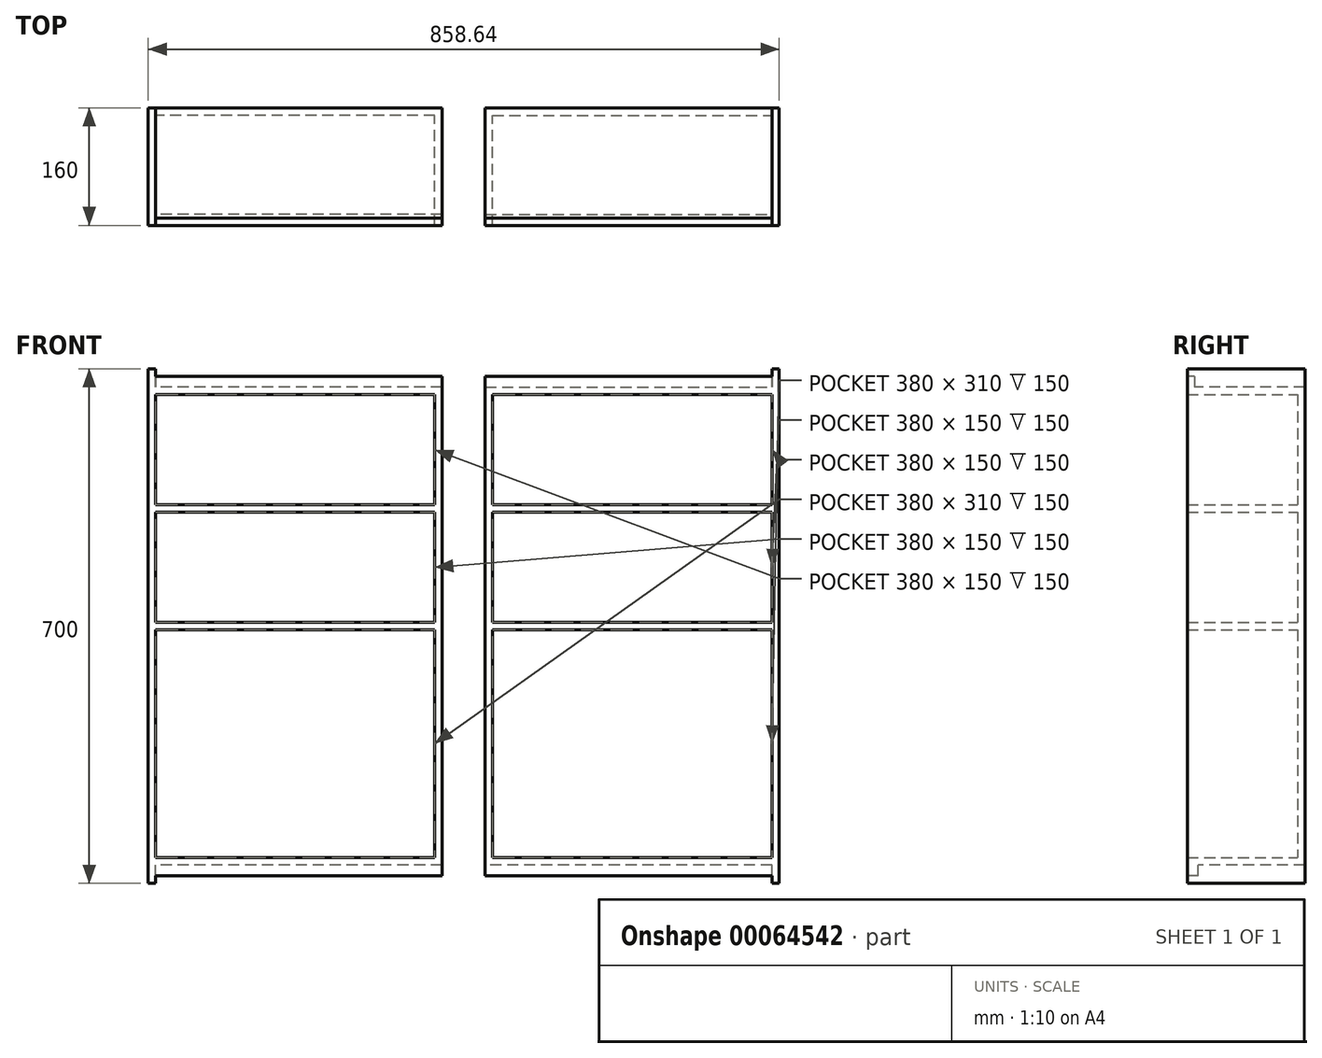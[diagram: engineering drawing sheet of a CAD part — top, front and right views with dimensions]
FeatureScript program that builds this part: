
annotation { "Feature Type Name" : "Feature", "Feature Type Description" : "" }
export const myFeature = defineFeature(function(context is Context, id is Id, definition is map)
    precondition{}
    {
        {
            var Q0;
            Q0=qCreatedBy(makeId("Front.planeOp"),FACE);
            var sketch = newSketch(context, id + "F0", { "sketchPlane" : qUnion([Q0])});
            skLineSegment(sketch, "E0.bottom", {"start": v(-429.32, 435.48) * mm, "end": v(-29.32, 435.48) * mm});
            skLineSegment(sketch, "E0.top", {"start": v(-429.32, -214.52) * mm, "end": v(-29.32, -214.52) * mm});
            skLineSegment(sketch, "E0.left", {"start": v(-429.32, 435.48) * mm, "end": v(-429.32, -214.52) * mm});
            skLineSegment(sketch, "E0.right", {"start": v(-29.32, 435.48) * mm, "end": v(-29.32, -214.52) * mm});
            skSolve(sketch);
        }
        {
            var Q0;
            Q0 = qSketchRegion(id + "F0", true);
            extrude(context, id + "F1", {"entities" : qUnion([Q0]), "depth" : 10 * mm});
        }
        {
            var Q0;
            Q0=makeQuery(id+"F1.opExtrude","CAP_FACE",FACE,{"disambiguationData":[OSD([sQuery(id+"F0.wireOp",EDGE,"E0.bottom"),sQuery(id+"F0.wireOp",EDGE,"E0.top"),sQuery(id+"F0.wireOp",EDGE,"E0.left"),sQuery(id+"F0.wireOp",EDGE,"E0.right")])],"isStart":false});
            var sketch = newSketch(context, id + "F2", { "sketchPlane" : qUnion([Q0])});
            skLineSegment(sketch, "E1", {"start": v(-429.32, 460.48) * mm, "end": v(-429.32, -239.52) * mm});
            skLineSegment(sketch, "E2", {"start": v(-429.32, -239.52) * mm, "end": v(-419.32, -239.52) * mm});
            skLineSegment(sketch, "E3", {"start": v(-419.32, -239.52) * mm, "end": v(-419.32, 460.48) * mm});
            skLineSegment(sketch, "E4", {"start": v(-419.32, 460.48) * mm, "end": v(-429.32, 460.48) * mm});
            skSolve(sketch);
        }
        {
            var Q0;
            {var subQ3=sQuery(id+"F2.wireOp",EDGE,"E4");Q0=makeQuery(id+"F2.imprint","IMPRINT",FACE,{"disambiguationData":[TD([[makeQuery(id+"F2.imprint","IMPRINT",EDGE,{"derivedFrom":subQ3}),1.0]])]});}
            var Q1;
            {var subQ0=sQuery(id+"F2.wireOp",EDGE,"E1");var subQ1=makeQuery(id+"F1.opExtrude","CAP_EDGE",EDGE,{"disambiguationData":[OSD([sQuery(id+"F0.wireOp",EDGE,"E0.bottom")])],"isStart":false});var subQ2=makeQuery(id+"F2.imprint","INTERSECT",VERTEX,{"derivedFrom":[subQ1,subQ0]});Q1=makeQuery(id+"F2.imprint","IMPRINT",FACE,{"disambiguationData":[TD([[makeQuery(id+"F2.imprint","IMPRINT",EDGE,{"disambiguationData":[TD([[subQ2,-1.0]])],"derivedFrom":subQ0}),1.0]])]});}
            var Q2;
            {var subQ3=sQuery(id+"F2.wireOp",EDGE,"E2");Q2=makeQuery(id+"F2.imprint","IMPRINT",FACE,{"disambiguationData":[TD([[makeQuery(id+"F2.imprint","IMPRINT",EDGE,{"derivedFrom":subQ3}),1.0]])]});}
            extrude(context, id + "F3", {"entities" : qUnion([Q0, Q1, Q2]), "operationType" : NewBodyOperationType.ADD, "depth" : 150 * mm, "hasSecondDirection" : true, "secondDirectionOppositeDirection" : true, "secondDirectionDepth" : 10 * mm});
        }
        {
            var Q0;
            Q0=makeQuery(id+"F1.opExtrude","CAP_FACE",FACE,{"disambiguationData":[OSD([sQuery(id+"F0.wireOp",EDGE,"E0.bottom"),sQuery(id+"F0.wireOp",EDGE,"E0.top"),sQuery(id+"F0.wireOp",EDGE,"E0.left"),sQuery(id+"F0.wireOp",EDGE,"E0.right")])],"isStart":false});
            var sketch = newSketch(context, id + "F4", { "sketchPlane" : qUnion([Q0])});
            skLineSegment(sketch, "E5", {"start": v(-419.32, 425.48) * mm, "end": v(-39.32, 425.48) * mm});
            skLineSegment(sketch, "E6", {"start": v(-39.32, 425.48) * mm, "end": v(-39.32, 275.48) * mm});
            skLineSegment(sketch, "E7", {"start": v(-39.32, 275.48) * mm, "end": v(-419.32, 275.48) * mm});
            skLineSegment(sketch, "E8", {"start": v(-419.32, 275.48) * mm, "end": v(-419.32, 265.48) * mm});
            skLineSegment(sketch, "E9", {"start": v(-419.32, 265.48) * mm, "end": v(-39.32, 265.48) * mm});
            skLineSegment(sketch, "E10", {"start": v(-39.32, 265.48) * mm, "end": v(-39.32, 115.48) * mm});
            skLineSegment(sketch, "E11", {"start": v(-39.32, 115.48) * mm, "end": v(-419.32, 115.48) * mm});
            skLineSegment(sketch, "E12", {"start": v(-419.32, 115.48) * mm, "end": v(-419.32, 105.48) * mm});
            skLineSegment(sketch, "E13", {"start": v(-419.32, 105.48) * mm, "end": v(-39.32, 105.48) * mm});
            skLineSegment(sketch, "E14", {"start": v(-39.32, 105.48) * mm, "end": v(-39.32, -204.52) * mm});
            skLineSegment(sketch, "E15", {"start": v(-39.32, -204.52) * mm, "end": v(-419.32, -204.52) * mm});
            skLineSegment(sketch, "E16", {"start": v(-419.32, -204.52) * mm, "end": v(-419.32, -214.52) * mm});
            skLineSegment(sketch, "E17", {"start": v(-419.32, -214.52) * mm, "end": v(-29.32, -214.52) * mm});
            skLineSegment(sketch, "E18", {"start": v(-29.32, -214.52) * mm, "end": v(-29.32, 435.48) * mm});
            skLineSegment(sketch, "E19", {"start": v(-29.32, 435.48) * mm, "end": v(-419.32, 435.48) * mm});
            skLineSegment(sketch, "E20", {"start": v(-419.32, 435.48) * mm, "end": v(-419.32, 425.48) * mm});
            skSolve(sketch);
        }
        {
            var Q0;
            Q0=makeQuery(id+"F4.imprint","IMPRINT",FACE,{"disambiguationData":[TD([[makeQuery(id+"F4.imprint","IMPRINT",EDGE,{"derivedFrom":sQuery(id+"F4.wireOp",EDGE,"E5")}),1.0]])]});
            extrude(context, id + "F5", {"entities" : qUnion([Q0]), "operationType" : NewBodyOperationType.ADD, "depth" : 150 * mm});
        }
        {
            var Q0;
            Q0=makeQuery(id+"F5.boolean.opBoolean","MERGE",FACE,{"derivedFrom":[makeQuery(id+"F1.opExtrude","SWEPT_FACE",FACE,{"disambiguationData":[OSD([sQuery(id+"F0.wireOp",EDGE,"E0.bottom")])]}),makeQuery(id+"F5.opExtrude","SWEPT_FACE",FACE,{"disambiguationData":[OSD([sQuery(id+"F4.wireOp",EDGE,"E19")])]})]});
            var sketch = newSketch(context, id + "F6", { "sketchPlane" : qUnion([Q0])});
            skLineSegment(sketch, "E21.bottom", {"start": v(-29.32, -160) * mm, "end": v(-419.32, -160) * mm});
            skLineSegment(sketch, "E21.top", {"start": v(-29.32, -150) * mm, "end": v(-419.32, -150) * mm});
            skLineSegment(sketch, "E21.left", {"start": v(-29.32, -160) * mm, "end": v(-29.32, -150) * mm});
            skLineSegment(sketch, "E21.right", {"start": v(-419.32, -160) * mm, "end": v(-419.32, -150) * mm});
            skSolve(sketch);
        }
        {
            var Q0;
            Q0 = qSketchRegion(id + "F6", true);
            extrude(context, id + "F7", {"entities" : qUnion([Q0]), "operationType" : NewBodyOperationType.ADD, "depth" : 15 * mm});
        }
        {
            var Q0;
            Q0=makeQuery(id+"F5.boolean.opBoolean","MERGE",FACE,{"derivedFrom":[makeQuery(id+"F1.opExtrude","SWEPT_FACE",FACE,{"disambiguationData":[OSD([sQuery(id+"F0.wireOp",EDGE,"E0.top")])]}),makeQuery(id+"F5.opExtrude","SWEPT_FACE",FACE,{"disambiguationData":[OSD([sQuery(id+"F4.wireOp",EDGE,"E17")])]})]});
            var sketch = newSketch(context, id + "F8", { "sketchPlane" : qUnion([Q0])});
            skLineSegment(sketch, "E22.bottom", {"start": v(-29.32, 160) * mm, "end": v(-419.32, 160) * mm});
            skLineSegment(sketch, "E22.top", {"start": v(-29.32, 145) * mm, "end": v(-419.32, 145) * mm});
            skLineSegment(sketch, "E22.left", {"start": v(-29.32, 160) * mm, "end": v(-29.32, 145) * mm});
            skLineSegment(sketch, "E22.right", {"start": v(-419.32, 160) * mm, "end": v(-419.32, 145) * mm});
            skSolve(sketch);
        }
        {
            var Q0;
            Q0=makeQuery(id+"F8.imprint","IMPRINT",FACE,{"disambiguationData":[TD([[makeQuery(id+"F8.imprint","IMPRINT",EDGE,{"derivedFrom":sQuery(id+"F8.wireOp",EDGE,"E22.bottom")}),-1.0]])]});
            extrude(context, id + "F9", {"entities" : qUnion([Q0]), "operationType" : NewBodyOperationType.ADD, "depth" : 15 * mm});
        }
        {
            var Q0;
            Q0=makeQuery(id+"F1.opExtrude","SWEPT_BODY",BODY,{"disambiguationData":[OSD([sQuery(id+"F0.wireOp",EDGE,"E0.bottom"),sQuery(id+"F0.wireOp",EDGE,"E0.top"),sQuery(id+"F0.wireOp",EDGE,"E0.left"),sQuery(id+"F0.wireOp",EDGE,"E0.right")])]});
            var Q1;
            Q1=qCreatedBy(makeId("Right.planeOp"),FACE);
            mirror(context, id + "F10", {"entities" : qUnion([Q0]), "mirrorPlane" : qUnion([Q1])});
        }
    });
